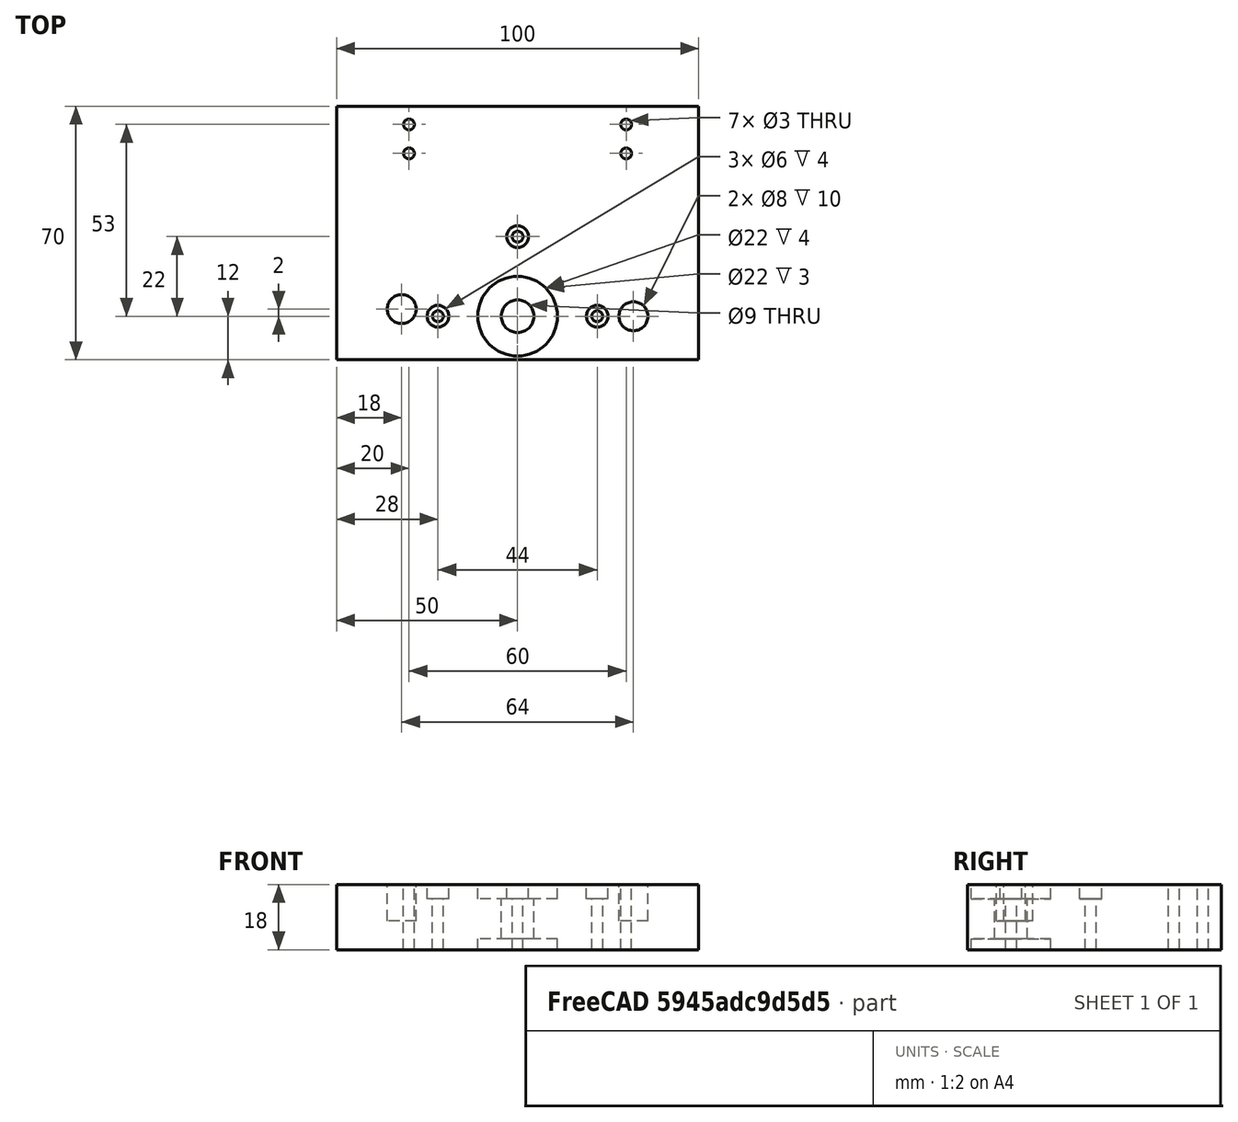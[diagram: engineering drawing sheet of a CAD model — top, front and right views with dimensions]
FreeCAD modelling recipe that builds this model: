
FCSTD DOCUMENT  (FreeCAD 0.17R13541 (Git))
Label: Z-Arriba
License: All rights reserved
LicenseURL: http://en.wikipedia.org/wiki/All_rights_reserved
objects: Part::Cylinder×15, Part::Cut×12, Part::MultiFuse×4, Part::Box×2
note: 33 computed .brp shape members not serialized (recipe doc carries the construction recipe); baked Part::Feature solids carry a one-line shape summary decoded from their .brp

FEATURE [Part::Box] Box  label="Izquierda"
  AttacherType = Attacher::AttachEngine3D
  Height = 18
  Length = 50
  Width = 70
FEATURE [Part::Cylinder] Cylinder  label="Cilindro-izquierda"
  Angle = 360
  AttacherType = Attacher::AttachEngine3D
  Height = 25
  Placement = pos=(18,12,8) rot=(0,0,1;0rad)
  Radius = 4
FEATURE [Part::Cylinder] Cylinder001  label="Cilindro00-Derecha"
  Angle = 360
  AttacherType = Attacher::AttachEngine3D
  Height = 25
  Placement = pos=(-18,12,8) rot=(0,0,1;0rad)
  Radius = 4
FEATURE [Part::Cut] Cut  label="Izquierda001"
  Base = -> Box
  Refine = true
  Tool = -> Cylinder
FEATURE [Part::Cylinder] Cylinder002  label="Cilindro"
  Angle = 360
  AttacherType = Attacher::AttachEngine3D
  Height = 25
  Placement = pos=(20,57,0) rot=(0,0,1;0rad)
  Radius = 1.5
FEATURE [Part::Cylinder] Cylinder003  label="Cilindro001"
  Angle = 360
  AttacherType = Attacher::AttachEngine3D
  Height = 25
  Placement = pos=(20,65,0) rot=(0,0,1;0rad)
  Radius = 1.5
FEATURE [Part::Cut] Cut002
  Base = -> Cut
  Refine = true
  Tool = -> Cylinder003
FEATURE [Part::Cut] Cut003  label="IzquierdaTerminado"
  Base = -> Cut002
  Refine = true
  Tool = -> Cylinder002
FEATURE [Part::Box] Box001  label="CuboCalato-Derecha"
  AttacherType = Attacher::AttachEngine3D
  Height = 18
  Length = 50
  Placement = pos=(-50,0,0) rot=(0,0,1;0rad)
  Width = 70
FEATURE [Part::Cut] Cut004  label="IzquierdaTerminado001"
  Base = -> Cut002
  Refine = true
  Tool = -> Cylinder002
FEATURE [Part::Cut] Cut005
  Base = -> Box001
  Refine = true
  Tool = -> Cylinder001
FEATURE [Part::Cylinder] Cylinder004  label="Cilindro002"
  Angle = 360
  AttacherType = Attacher::AttachEngine3D
  Height = 25
  Placement = pos=(-20,57,0) rot=(0,0,1;0rad)
  Radius = 1.5
FEATURE [Part::Cylinder] Cylinder005  label="Cilindro003"
  Angle = 360
  AttacherType = Attacher::AttachEngine3D
  Height = 25
  Placement = pos=(-20,65,0) rot=(0,0,1;0rad)
  Radius = 1.5
FEATURE [Part::Cut] Cut006
  Base = -> Cut005
  Refine = true
  Tool = -> Cylinder004
FEATURE [Part::Cut] Cut007
  Base = -> Cut006
  Placement = pos=(100,0,0) rot=(0,0,1;0rad)
  Refine = true
  Tool = -> Cylinder005
FEATURE [Part::MultiFuse] Fusion
  Refine = true
  Shapes = -> [Cut003,Cut004]
FEATURE [Part::MultiFuse] Fusion001  label="Z-Arriba"
  Refine = true
  Shapes = -> [Cut007,Fusion]
FEATURE [Part::Cylinder] Cylinder006  label="Cilindro004"
  Angle = 360
  AttacherType = Attacher::AttachEngine3D
  Height = 25
  Placement = pos=(28,12,0) rot=(0,0,1;0rad)
  Radius = 1.5
FEATURE [Part::Cylinder] Cylinder007  label="Cilindro005"
  Angle = 360
  AttacherType = Attacher::AttachEngine3D
  Height = 25
  Placement = pos=(72,12,0) rot=(0,0,1;0rad)
  Radius = 1.5
FEATURE [Part::Cylinder] Cylinder008  label="Cilindro006"
  Angle = 360
  AttacherType = Attacher::AttachEngine3D
  Height = 25
  Placement = pos=(50,34,0) rot=(0,0,1;0rad)
  Radius = 1.5
FEATURE [Part::MultiFuse] Fusion002
  Refine = true
  Shapes = -> [Cylinder008,Cylinder007,Cylinder006]
FEATURE [Part::Cut] Cut008
  Base = -> Fusion001
  Refine = true
  Tool = -> Fusion002
FEATURE [Part::Cylinder] Cylinder009  label="Cilindro007"
  Angle = 360
  AttacherType = Attacher::AttachEngine3D
  Height = 25
  Placement = pos=(50,12,14) rot=(0,0,1;0rad)
  Radius = 11
FEATURE [Part::Cut] Cut009
  Base = -> Cut008
  Refine = true
  Tool = -> Cylinder009
FEATURE [Part::Cylinder] Cylinder010  label="Cilindro008"
  Angle = 360
  AttacherType = Attacher::AttachEngine3D
  Height = 25
  Placement = pos=(28,12,14) rot=(0,0,1;0rad)
  Radius = 3
FEATURE [Part::Cylinder] Cylinder011  label="Cilindro009"
  Angle = 360
  AttacherType = Attacher::AttachEngine3D
  Height = 25
  Placement = pos=(72,12,14) rot=(0,0,1;0rad)
  Radius = 3
FEATURE [Part::Cylinder] Cylinder012  label="Cilindro010"
  Angle = 360
  AttacherType = Attacher::AttachEngine3D
  Height = 25
  Placement = pos=(50,34,14) rot=(0,0,1;0rad)
  Radius = 3
FEATURE [Part::MultiFuse] Fusion003
  Refine = true
  Shapes = -> [Cylinder012,Cylinder011,Cylinder010]
FEATURE [Part::Cut] Cut010
  Base = -> Cut009
  Refine = true
  Tool = -> Fusion003
FEATURE [Part::Cylinder] Cylinder013  label="Cilindro011"
  Angle = 360
  AttacherType = Attacher::AttachEngine3D
  Height = 25
  Placement = pos=(50,12,0) rot=(0,0,1;0rad)
  Radius = 4.5
FEATURE [Part::Cut] Cut011
  Base = -> Cut010
  Refine = true
  Tool = -> Cylinder013
FEATURE [Part::Cylinder] Cylinder014  label="Cilindro012"
  Angle = 360
  AttacherType = Attacher::AttachEngine3D
  Height = 3
  Placement = pos=(50,12,0) rot=(0,0,1;0rad)
  Radius = 11
FEATURE [Part::Cut] Cut012
  Base = -> Cut011
  Refine = true
  Tool = -> Cylinder014
